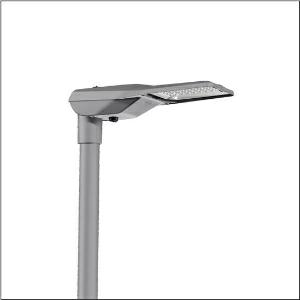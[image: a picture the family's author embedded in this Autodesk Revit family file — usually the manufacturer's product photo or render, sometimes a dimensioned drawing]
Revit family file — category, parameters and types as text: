
# Revit family: streetlight_sl_21_iq_mini___st1_0a_5xe2d51y08gb_2a2c
name_source: partatom
category: Lighting Fixtures
units: mm (PartAtom-declared; Revit-internal decimal feet)

## family parameters
Cut with Voids When Loaded = No
Host = Face
Light Source = No
Part Type = Normal
Room Calculation Point = No
Round Connector Dimension = Use Diameter
Shared = No

## types (1)
- --- (1 x LED, 5260 lm, 39.8 W, 3000K)
    Apparent Load = 40 VA
    CIE Flux Codes = 37 72 97 100 100
    Color Rendering = 80
    Color Temperature = 3000K
    Default Elevation = 1800 mm
    Description = Streetlight SL 21 iQ mini, mast luminaire, primary light control with lens, of PMMA, primary optical cover: cover, of toughened safety glass, transparent, light distribution: ST1.0a, light emission: direct distribution, primary light characteristic: asymmetric, installation type: post-top, side-entry, LED, High Power LED, rated luminous flux: 5.260lm, luminous efficacy: 132lm/W, light colour: 830, colour temperature: 3000K, control: presetting dimming logarithmic, Street-Remote, Auto-Match, Temp-Guard, Lumen-Switch, Night-Set, Smart-Wire, Light-Fading, Desk-Remote (wireless, voltage-free reading and setting of iQ features in the workshop via application-optimized NFC function/RFID function), optimised constant luminous flux control (CLO 2.0), mains connection: 220..240V, AC, 50/60Hz, start of lifetime: 40W, end of service life: 41W, reduction: 18W, luminaire housing, of diecast aluminium, powder-coated, Siteco® metallic grey (DB 702S), corrosivity category C5 mid according to DIN EN ISO 12944, please order mast flange separately, inclination adjustable: 0°, 5°, 10°, 15°, sealing non-destructively replaceable, multi-level sealing system, length: 628mm, width: 235mm, height: 110mm, mast flange for spigot size: 42mm (side-entry): 5XC10008XM4, 60/48mm (side-entry/post-top): 5XC10108XM2, 76/60mm (side-entry/post-top): 5XC10108XM1, Smart Interface below and above, protection rating (complete): IP66, insulation class (complete): insulation class II (safety insulation), certification: CE, ENEC, ENEC+, VDE, impact resistance: IK09, permissible operating ambient temperature for outdoor applications: -40..+50°C, standard-compliant lighting for roads and squares, packaging unit: 1 piece

Light Distribution: ST1.0a
    Height = 110 mm
    Lamp = 1 x LED
    Lamp Light Flux = 5260 lm
    Lamp Power = 39.8 W
    Lamp count = 1
    Length = 625 mm
    Luminous efficacy = 132 lm/W
    Manufacturer = Siteco
    ModVariant = No
    Model = 5XE2D51Y08GB
    Number of Poles = 1
    OnlyDefault = Yes
    Power Factor = 1
    Product Name = Streetlight SL 21 iQ mini | ST1.0a
    Product group = mast luminaire | pylon top
    ProductGroupID = 6100
    Protection Class = Protection class II
    Protection Degree = IP 66
    RLX_Detail_Level = 1
    RLX_Emergency_Light_Flux = 0 lm
    RLX_Emergency_Type = 0
    RLX_Emergency_Type_DB = No
    RlxData = <blob elided: 92933 chars, md5=750d15cb>
    Socket = socket
    Standby Power = 0 W
    System Light Flux = 5260 lm
    System Power = 40 W
    Type Comments = factory setting: luminous flux: 100 % | dim-lin: 254 | 800 mA
    Type Image = l_1003514.jpg
    URL = http://relux.com
    VarID = @adj_044875
    Voltage = 0 V
    Weight = 0.00 kg
    Width = 234 mm

## geometry (parser evidence)
native form markers: Blend x4, Sweep x11
no freeform markers — native parametric forms only
